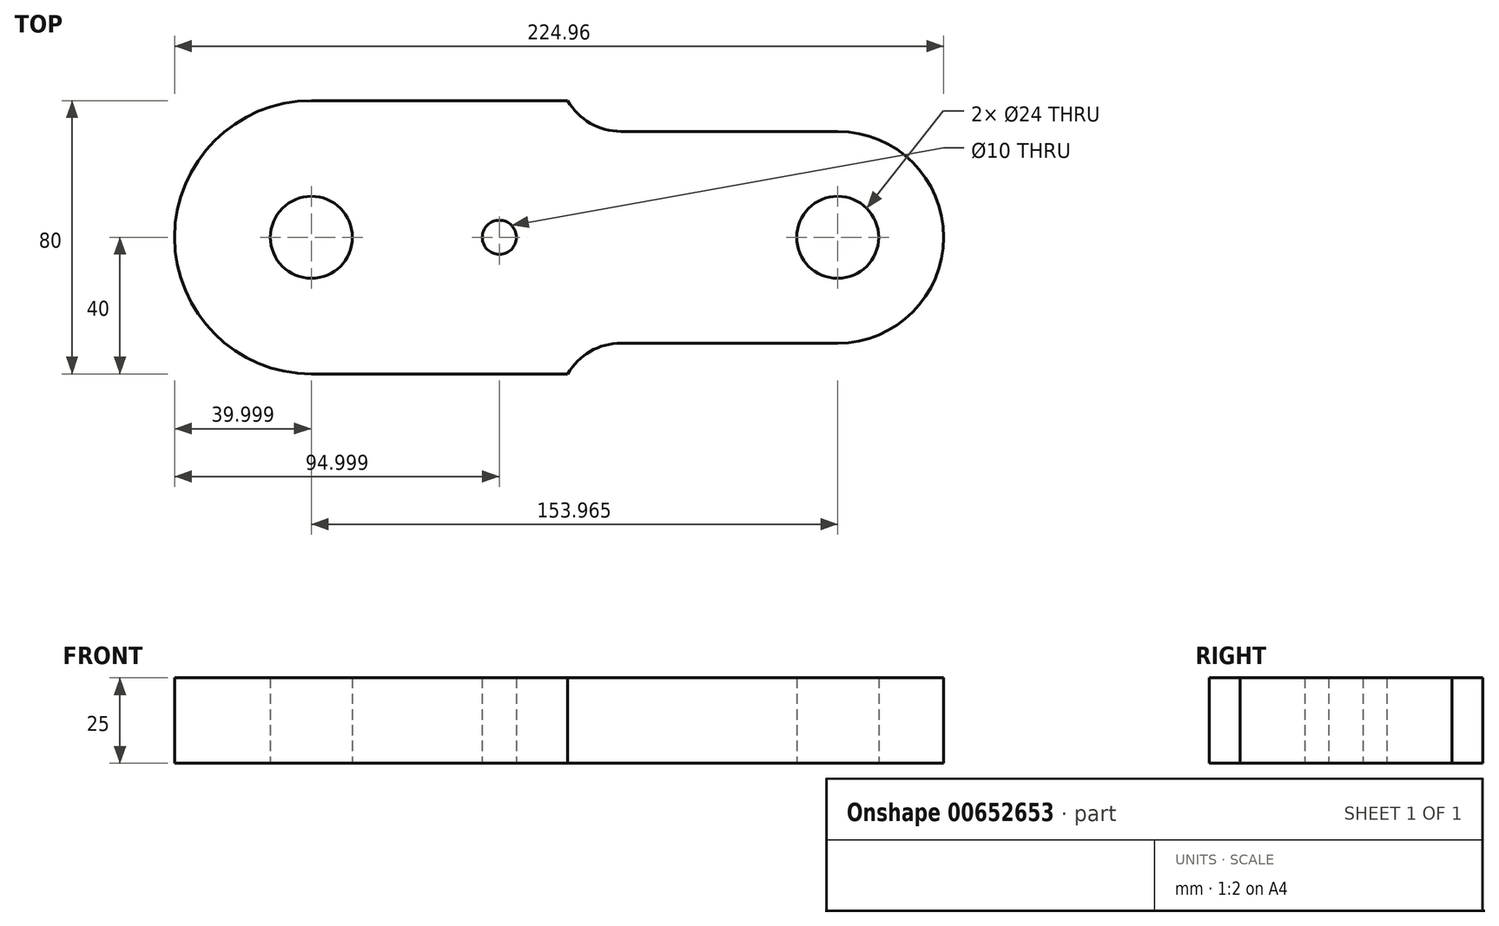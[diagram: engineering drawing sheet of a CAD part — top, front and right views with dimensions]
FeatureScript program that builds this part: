
annotation { "Feature Type Name" : "Feature", "Feature Type Description" : "" }
export const myFeature = defineFeature(function(context is Context, id is Id, definition is map)
    precondition{}
    {
        {
            var Q0;
            Q0=qCreatedBy(makeId("Top.planeOp"),FACE);
            var sketch = newSketch(context, id + "F0", { "sketchPlane" : qUnion([Q0])});
            skArc(sketch, "E0", {"start": v(-124.05, 40) * mm, "mid": v(-164.05, 0) * mm, "end": v(-124.05, -40) * mm});
            skLineSegment(sketch, "E1", {"start": v(-124.05, 40) * mm, "end": v(-49.05, 40) * mm});
            skLineSegment(sketch, "E2", {"start": v(-124.05, -40) * mm, "end": v(-49.05, -40) * mm});
            skLineSegment(sketch, "E3", {"start": v(-124.05, 67.99) * mm, "end": v(-124.05, -51.89) * mm, "construction": true});
            skCircle(sketch, "E4", {"center": v(-124.05, 0) * mm, "radius": 12 * mm});
            skCircle(sketch, "E5", {"center": v(-69.05, 0) * mm, "radius": 5 * mm});
            skArc(sketch, "E6", {"start": v(-33.46, -31) * mm, "mid": v(-42.46, -33.41) * mm, "end": v(-49.05, -40) * mm});
            skLineSegment(sketch, "E7", {"start": v(-176.23, 0) * mm, "end": v(199.66, 0) * mm, "construction": true});
            skArc(sketch, "E8.MirrorCS", {"start": v(-33.46, 31) * mm, "mid": v(-42.46, 33.41) * mm, "end": v(-49.05, 40) * mm});
            skLineSegment(sketch, "E9.MirrorCS", {"start": v(-33.46, 31) * mm, "end": v(29.91, 31) * mm});
            skLineSegment(sketch, "E10.MirrorCS", {"start": v(-33.46, -31) * mm, "end": v(29.91, -31) * mm});
            skPoint(sketch, "E11.visualSharp", {"position": v(-33.46, 31) * mm});
            skLineSegment(sketch, "E11.filletArc", {"start": v(-33.46, 31) * mm, "end": v(-33.46, 31) * mm});
            skArc(sketch, "E12", {"start": v(29.91, -31) * mm, "mid": v(60.91, 0) * mm, "end": v(29.91, 31) * mm});
            skPoint(sketch, "E13.start.orphan", {"position": v(29.91, 60.09) * mm});
            skPoint(sketch, "E14.trimOffspring.end.orphan", {"position": v(29.91, -72.62) * mm});
            skPoint(sketch, "E15.orphan", {"position": v(-33.46, -14.02) * mm});
            skCircle(sketch, "E16", {"center": v(29.91, 0) * mm, "radius": 12 * mm});
            skSolve(sketch);
        }
        {
            var Q0;
            Q0 = qSketchRegion(id + "F0", true);
            extrude(context, id + "F1", {"entities" : qUnion([Q0]), "depth" : 25 * mm, "offsetDistance" : 25 * mm});
        }
    });
